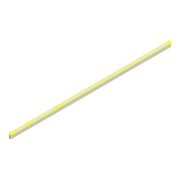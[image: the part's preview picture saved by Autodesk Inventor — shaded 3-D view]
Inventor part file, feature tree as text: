
AUTODESK INVENTOR PART (.ipt)
format: ipt  version: 2022 (Build 260153000, 153)  size: 97,792 bytes
history: native  units: mm
features: sketch x2, extrude x1, projected_geometry x1
ambient origin geometry x8: Origin, YZ Plane, XZ Plane, XY Plane, X Axis, Y Axis, Z Axis, Center Point
bodies: Solid1 (feature_tree)
feature tree (4):
  extrude  "Extrusion1"  Depth=6.0mm
  sketch  "Sketch2"  dims[d2=3.0mm d3=3.0mm d4=8.0mm d5=0.0mm d6=3.0mm d7=101.938mm d8=3.0mm d9=37.934mm]
  sketch  "Sketch1"  dims[d0=347.765mm d1=6.0mm]
  projected_geometry  "Projected Loop1"
